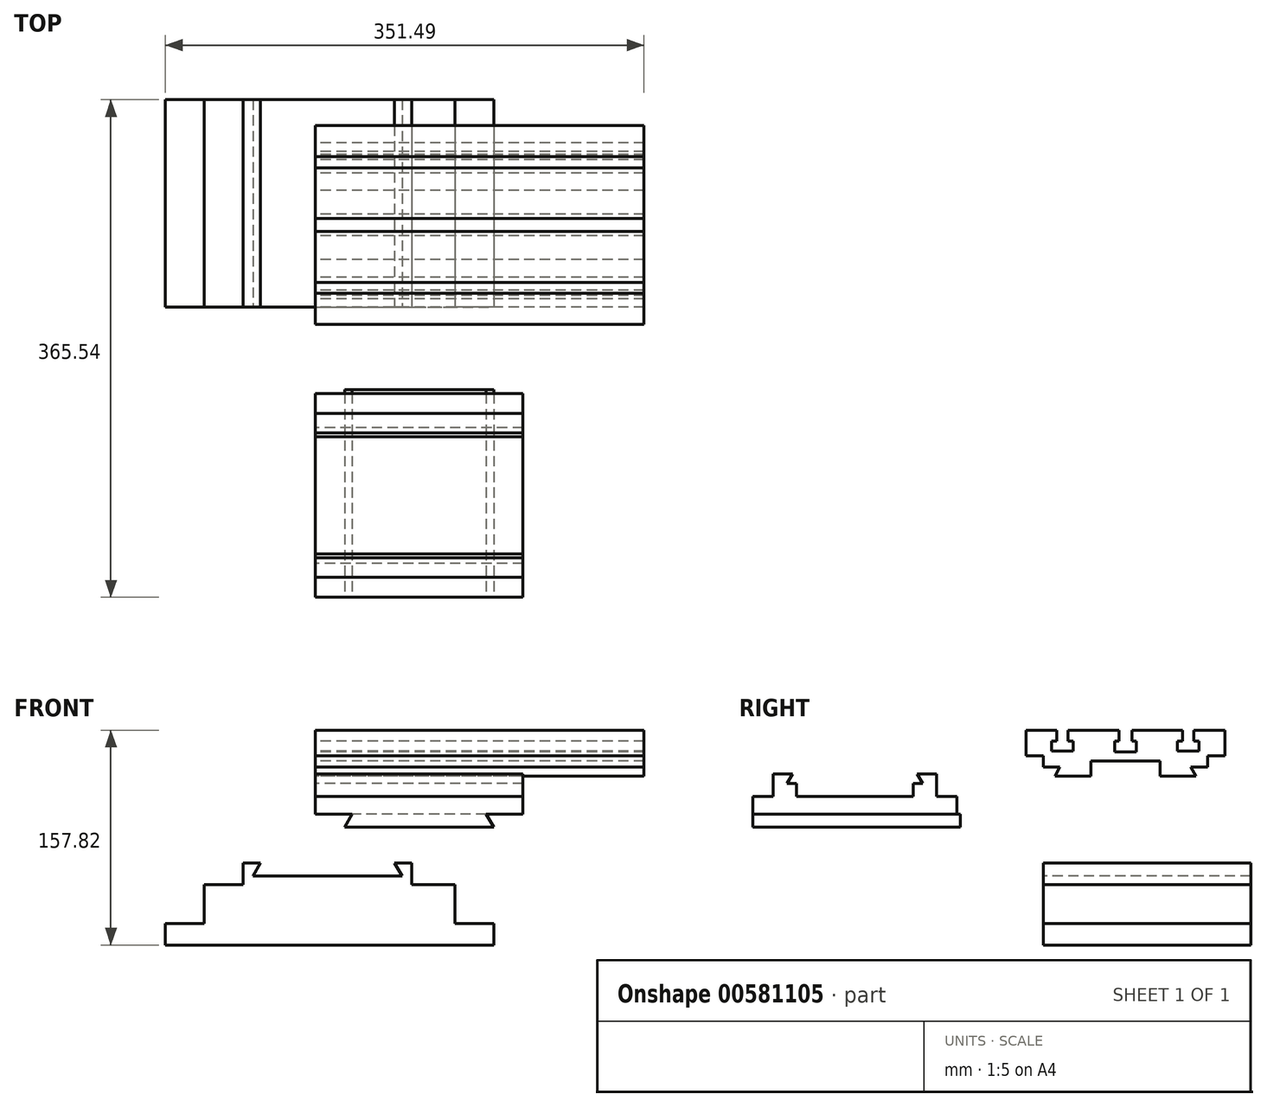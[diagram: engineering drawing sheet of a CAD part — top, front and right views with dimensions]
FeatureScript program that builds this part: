
annotation { "Feature Type Name" : "Feature", "Feature Type Description" : "" }
export const myFeature = defineFeature(function(context is Context, id is Id, definition is map)
    precondition{}
    {
        {
            var Q0;
            Q0=qCreatedBy(makeId("Front.planeOp"),FACE);
            var sketch = newSketch(context, id + "F0", { "sketchPlane" : qUnion([Q0])});
            skLineSegment(sketch, "E0", {"start": v(-110.2, -62.33) * mm, "end": v(131.1, -62.33) * mm});
            skLineSegment(sketch, "E1", {"start": v(131.1, -62.33) * mm, "end": v(131.1, -46.46) * mm});
            skLineSegment(sketch, "E2", {"start": v(131.1, -46.46) * mm, "end": v(102.53, -46.46) * mm});
            skLineSegment(sketch, "E3", {"start": v(-110.2, -46.46) * mm, "end": v(-110.2, -62.33) * mm});
            skLineSegment(sketch, "E4", {"start": v(-81.62, -46.46) * mm, "end": v(-81.62, -17.88) * mm});
            skLineSegment(sketch, "E5", {"start": v(-81.62, -17.88) * mm, "end": v(-53.04, -17.88) * mm});
            skLineSegment(sketch, "E6", {"start": v(102.53, -17.88) * mm, "end": v(102.53, -46.46) * mm});
            skLineSegment(sketch, "E7", {"start": v(-53.04, -17.88) * mm, "end": v(-53.04, -2) * mm});
            skLineSegment(sketch, "E8", {"start": v(-53.04, -2) * mm, "end": v(-40.34, -2) * mm});
            skLineSegment(sketch, "E9", {"start": v(-40.34, -2) * mm, "end": v(-45.84, -11.53) * mm});
            skLineSegment(sketch, "E10", {"start": v(-45.84, -11.53) * mm, "end": v(63.58, -11.53) * mm});
            skLineSegment(sketch, "E11", {"start": v(63.58, -11.53) * mm, "end": v(58.08, -2) * mm});
            skLineSegment(sketch, "E12", {"start": v(58.08, -2) * mm, "end": v(70.78, -2) * mm});
            skLineSegment(sketch, "E13", {"start": v(70.78, -2) * mm, "end": v(70.78, -17.88) * mm});
            skLineSegment(sketch, "E14.trimOffspring", {"start": v(70.78, -17.88) * mm, "end": v(102.53, -17.88) * mm});
            skLineSegment(sketch, "E15.trimOffspring", {"start": v(-81.62, -46.46) * mm, "end": v(-110.2, -46.46) * mm});
            skSolve(sketch);
        }
        {
            var Q0;
            Q0=makeQuery(id+"F0.imprint","IMPRINT",FACE,{"disambiguationData":[TD([[makeQuery(id+"F0.imprint","IMPRINT",EDGE,{"derivedFrom":sQuery(id+"F0.wireOp",EDGE,"E0")}),1.0]])]});
            extrude(context, id + "F1", {"entities" : qUnion([Q0]), "oppositeDirection" : true, "depth" : 152.4 * mm, "offsetDistance" : 25.4 * mm});
        }
        {
            var Q0;
            Q0=qCreatedBy(makeId("Right.planeOp"),FACE);
            var sketch = newSketch(context, id + "F2", { "sketchPlane" : qUnion([Q0])});
            skLineSegment(sketch, "E16", {"start": v(8.54, 61.81) * mm, "end": v(34.93, 61.81) * mm});
            skLineSegment(sketch, "E17", {"start": v(112.1, 61.81) * mm, "end": v(108.34, 68.34) * mm});
            skLineSegment(sketch, "E18", {"start": v(12.31, 68.34) * mm, "end": v(8.54, 61.81) * mm});
            skLineSegment(sketch, "E19.top", {"start": v(34.93, 72.93) * mm, "end": v(85.73, 72.93) * mm});
            skLineSegment(sketch, "E19.left", {"start": v(34.93, 61.81) * mm, "end": v(34.93, 72.93) * mm});
            skLineSegment(sketch, "E19.right", {"start": v(85.73, 61.81) * mm, "end": v(85.73, 72.93) * mm});
            skLineSegment(sketch, "E20.bottom", {"start": v(120.65, 68.34) * mm, "end": v(108.34, 68.34) * mm});
            skLineSegment(sketch, "E20.left", {"start": v(120.65, 68.34) * mm, "end": v(120.65, 76.52) * mm});
            skLineSegment(sketch, "E20.right", {"start": v(0, 68.34) * mm, "end": v(0, 76.52) * mm});
            skLineSegment(sketch, "E21.bottom", {"start": v(133.35, 76.52) * mm, "end": v(120.65, 76.52) * mm});
            skLineSegment(sketch, "E21.top", {"start": v(133.35, 95.5) * mm, "end": v(110.6, 95.5) * mm});
            skLineSegment(sketch, "E21.left", {"start": v(133.35, 76.52) * mm, "end": v(133.35, 95.5) * mm});
            skLineSegment(sketch, "E21.right", {"start": v(-12.7, 76.52) * mm, "end": v(-12.7, 95.5) * mm});
            skLineSegment(sketch, "E22.left", {"start": v(55.56, 95.5) * mm, "end": v(55.56, 87.56) * mm});
            skLineSegment(sketch, "E22.right", {"start": v(65.09, 95.5) * mm, "end": v(65.09, 87.56) * mm});
            skLineSegment(sketch, "E23.bottom", {"start": v(52.39, 87.56) * mm, "end": v(55.56, 87.56) * mm});
            skLineSegment(sketch, "E23.top", {"start": v(52.39, 79.62) * mm, "end": v(68.26, 79.62) * mm});
            skLineSegment(sketch, "E23.left", {"start": v(52.39, 87.56) * mm, "end": v(52.39, 79.62) * mm});
            skLineSegment(sketch, "E23.right", {"start": v(68.26, 87.56) * mm, "end": v(68.26, 79.62) * mm});
            skLineSegment(sketch, "E24.trimOffspring", {"start": v(65.09, 87.56) * mm, "end": v(68.26, 87.56) * mm});
            skLineSegment(sketch, "E25.trimOffspring", {"start": v(12.31, 68.34) * mm, "end": v(0, 68.34) * mm});
            skPoint(sketch, "E26", {"position": v(60.33, 61.81) * mm});
            skPoint(sketch, "E27", {"position": v(60.33, 76.52) * mm});
            skLineSegment(sketch, "E28.trimOffspring", {"start": v(0, 76.52) * mm, "end": v(-12.7, 76.52) * mm});
            skLineSegment(sketch, "E29.trimOffspring", {"start": v(85.73, 61.81) * mm, "end": v(112.1, 61.81) * mm});
            skPoint(sketch, "E30", {"position": v(60.32, 95.5) * mm});
            skLineSegment(sketch, "E31.trimOffspring", {"start": v(55.56, 95.5) * mm, "end": v(18.26, 95.5) * mm});
            skLineSegment(sketch, "E32.left", {"start": v(10.06, 95.5) * mm, "end": v(10.06, 87.37) * mm});
            skLineSegment(sketch, "E32.right", {"start": v(18.26, 95.5) * mm, "end": v(18.26, 87.37) * mm});
            skLineSegment(sketch, "E33.bottom", {"start": v(6.22, 87.37) * mm, "end": v(10.06, 87.37) * mm});
            skLineSegment(sketch, "E33.top", {"start": v(6.22, 80.13) * mm, "end": v(22.1, 80.13) * mm});
            skLineSegment(sketch, "E33.left", {"start": v(6.22, 87.37) * mm, "end": v(6.22, 80.13) * mm});
            skLineSegment(sketch, "E33.right", {"start": v(22.1, 87.37) * mm, "end": v(22.1, 80.13) * mm});
            skLineSegment(sketch, "E34.trimOffspring", {"start": v(18.26, 87.37) * mm, "end": v(22.1, 87.37) * mm});
            skLineSegment(sketch, "E35.trimOffspring", {"start": v(10.06, 95.5) * mm, "end": v(-12.7, 95.5) * mm});
            skLineSegment(sketch, "E36.left", {"start": v(102.39, 95.5) * mm, "end": v(102.39, 87.37) * mm});
            skLineSegment(sketch, "E36.right", {"start": v(110.6, 95.5) * mm, "end": v(110.6, 87.37) * mm});
            skLineSegment(sketch, "E37.bottom", {"start": v(98.55, 87.37) * mm, "end": v(102.39, 87.37) * mm});
            skLineSegment(sketch, "E37.top", {"start": v(98.55, 80.13) * mm, "end": v(114.43, 80.13) * mm});
            skLineSegment(sketch, "E37.left", {"start": v(98.55, 87.37) * mm, "end": v(98.55, 80.13) * mm});
            skLineSegment(sketch, "E37.right", {"start": v(114.43, 87.37) * mm, "end": v(114.43, 80.13) * mm});
            skLineSegment(sketch, "E38.trimOffspring", {"start": v(110.6, 87.37) * mm, "end": v(114.43, 87.37) * mm});
            skLineSegment(sketch, "E39.trimOffspring", {"start": v(102.39, 95.5) * mm, "end": v(65.09, 95.5) * mm});
            skSolve(sketch);
        }
        {
            var Q0;
            Q0=makeQuery(id+"F2.imprint","IMPRINT",FACE,{"disambiguationData":[TD([[makeQuery(id+"F2.imprint","IMPRINT",EDGE,{"derivedFrom":sQuery(id+"F2.wireOp",EDGE,"E16")}),1.0]])]});
            extrude(context, id + "F3", {"entities" : qUnion([Q0]), "depth" : 241.3 * mm, "offsetDistance" : 25.4 * mm});
        }
        {
            var Q0;
            Q0=qCreatedBy(makeId("Right.planeOp"),FACE);
            var sketch = newSketch(context, id + "F4", { "sketchPlane" : qUnion([Q0])});
            skLineSegment(sketch, "E40.bottom", {"start": v(-213.14, 33.68) * mm, "end": v(-63.4, 33.68) * mm});
            skLineSegment(sketch, "E40.top", {"start": v(-213.14, 46.64) * mm, "end": v(-198.33, 46.64) * mm});
            skLineSegment(sketch, "E40.left", {"start": v(-213.14, 33.68) * mm, "end": v(-213.14, 46.64) * mm});
            skLineSegment(sketch, "E40.right", {"start": v(-63.4, 33.68) * mm, "end": v(-63.4, 46.64) * mm});
            skLineSegment(sketch, "E41", {"start": v(-198.33, 46.64) * mm, "end": v(-198.33, 63.4) * mm});
            skLineSegment(sketch, "E42", {"start": v(-198.33, 63.4) * mm, "end": v(-184.04, 63.4) * mm});
            skLineSegment(sketch, "E43", {"start": v(-184.04, 63.4) * mm, "end": v(-188.16, 56.27) * mm});
            skLineSegment(sketch, "E44", {"start": v(-188.16, 56.27) * mm, "end": v(-181.23, 56.27) * mm});
            skLineSegment(sketch, "E45", {"start": v(-88.38, 56.27) * mm, "end": v(-92.5, 63.4) * mm});
            skLineSegment(sketch, "E46", {"start": v(-92.5, 63.4) * mm, "end": v(-78.21, 63.4) * mm});
            skLineSegment(sketch, "E47", {"start": v(-78.21, 63.4) * mm, "end": v(-78.21, 46.64) * mm});
            skLineSegment(sketch, "E48.bottom", {"start": v(-181.23, 46.64) * mm, "end": v(-95.3, 46.64) * mm});
            skLineSegment(sketch, "E48.left", {"start": v(-181.23, 46.64) * mm, "end": v(-181.23, 56.27) * mm});
            skLineSegment(sketch, "E48.right", {"start": v(-95.3, 46.64) * mm, "end": v(-95.3, 56.27) * mm});
            skLineSegment(sketch, "E49.trimOffspring", {"start": v(-95.3, 56.27) * mm, "end": v(-88.38, 56.27) * mm});
            skLineSegment(sketch, "E50.trimOffspring", {"start": v(-78.21, 46.64) * mm, "end": v(-63.4, 46.64) * mm});
            skSolve(sketch);
        }
        {
            var Q0;
            Q0=makeQuery(id+"F4.imprint","IMPRINT",FACE,{"disambiguationData":[TD([[makeQuery(id+"F4.imprint","IMPRINT",EDGE,{"derivedFrom":sQuery(id+"F4.wireOp",EDGE,"E40.bottom")}),1.0]])]});
            extrude(context, id + "F5", {"entities" : qUnion([Q0]), "depth" : 152.4 * mm, "offsetDistance" : 25.4 * mm});
        }
        {
            var Q0;
            Q0=makeQuery(id+"F5.opExtrude","SWEPT_FACE",FACE,{"disambiguationData":[OSD([sQuery(id+"F4.wireOp",EDGE,"E40.left")])]});
            var sketch = newSketch(context, id + "F6", { "sketchPlane" : qUnion([Q0])});
            skLineSegment(sketch, "E51", {"start": v(26.99, 33.68) * mm, "end": v(125.41, 33.68) * mm});
            skLineSegment(sketch, "E52", {"start": v(125.41, 33.68) * mm, "end": v(130.91, 24.16) * mm});
            skLineSegment(sketch, "E53", {"start": v(21.49, 24.16) * mm, "end": v(130.91, 24.16) * mm});
            skLineSegment(sketch, "E54", {"start": v(21.49, 24.16) * mm, "end": v(26.99, 33.68) * mm});
            skSolve(sketch);
        }
        {
            var Q0;
            Q0=makeQuery(id+"F6.imprint","IMPRINT",FACE,{"disambiguationData":[TD([[makeQuery(id+"F6.imprint","IMPRINT",EDGE,{"derivedFrom":sQuery(id+"F6.wireOp",EDGE,"E51")}),1.0]])]});
            extrude(context, id + "F7", {"entities" : qUnion([Q0]), "operationType" : NewBodyOperationType.ADD, "oppositeDirection" : true, "depth" : 152.4 * mm, "offsetDistance" : 25.4 * mm});
        }
    });
